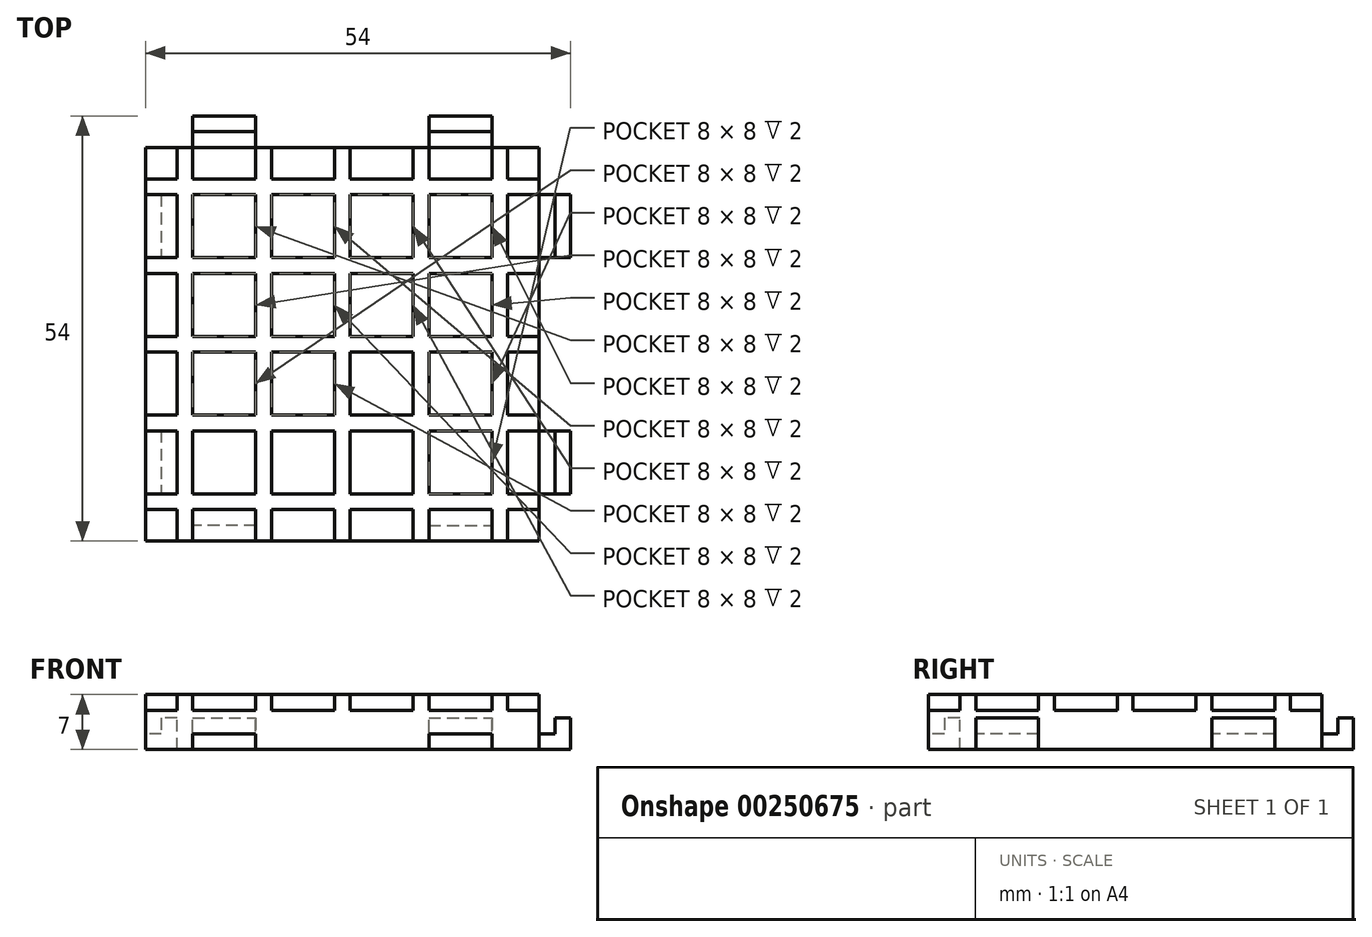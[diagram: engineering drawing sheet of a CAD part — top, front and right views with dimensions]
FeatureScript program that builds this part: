
annotation { "Feature Type Name" : "Feature", "Feature Type Description" : "" }
export const myFeature = defineFeature(function(context is Context, id is Id, definition is map)
    precondition{}
    {
        {
            var Q0;
            Q0=qCreatedBy(makeId("Top.planeOp"),FACE);
            var sketch = newSketch(context, id + "F0", { "sketchPlane" : qUnion([Q0])});
            skLineSegment(sketch, "E0.bottom", {"start": v(-29.37, 40.47) * mm, "end": v(20.63, 40.47) * mm});
            skLineSegment(sketch, "E0.top", {"start": v(-29.37, -9.53) * mm, "end": v(20.63, -9.53) * mm});
            skLineSegment(sketch, "E0.left", {"start": v(-29.37, 40.47) * mm, "end": v(-29.37, -9.53) * mm});
            skLineSegment(sketch, "E0.right", {"start": v(20.63, 40.47) * mm, "end": v(20.63, -9.53) * mm});
            skSolve(sketch);
        }
        {
            var Q0;
            Q0 = qSketchRegion(id + "F0", true);
            extrude(context, id + "F1", {"entities" : qUnion([Q0]), "depth" : 5 * mm});
        }
        {
            var Q0;
            Q0=makeQuery(id+"F1.opExtrude","CAP_FACE",FACE,{"disambiguationData":[OSD([sQuery(id+"F0.wireOp",EDGE,"E0.bottom"),sQuery(id+"F0.wireOp",EDGE,"E0.top"),sQuery(id+"F0.wireOp",EDGE,"E0.left"),sQuery(id+"F0.wireOp",EDGE,"E0.right")])],"isStart":false});
            var sketch = newSketch(context, id + "F2", { "sketchPlane" : qUnion([Q0])});
            skLineSegment(sketch, "E1.bottom", {"start": v(-29.37, -5.53) * mm, "end": v(20.63, -5.53) * mm});
            skLineSegment(sketch, "E1.top", {"start": v(-29.37, -3.53) * mm, "end": v(20.63, -3.53) * mm});
            skLineSegment(sketch, "E1.left", {"start": v(-29.37, -5.53) * mm, "end": v(-29.37, -3.53) * mm});
            skLineSegment(sketch, "E1.right", {"start": v(20.63, -5.53) * mm, "end": v(20.63, -3.53) * mm});
            skLineSegment(sketch, "E2.bottom", {"start": v(-29.37, 4.47) * mm, "end": v(20.63, 4.47) * mm});
            skLineSegment(sketch, "E2.top", {"start": v(-29.37, 6.47) * mm, "end": v(20.63, 6.47) * mm});
            skLineSegment(sketch, "E2.left", {"start": v(-29.37, 4.47) * mm, "end": v(-29.37, 6.47) * mm});
            skLineSegment(sketch, "E2.right", {"start": v(20.63, 4.47) * mm, "end": v(20.63, 6.47) * mm});
            skLineSegment(sketch, "E3.bottom", {"start": v(-29.37, 14.47) * mm, "end": v(20.63, 14.47) * mm});
            skLineSegment(sketch, "E3.top", {"start": v(-29.37, 16.47) * mm, "end": v(20.63, 16.47) * mm});
            skLineSegment(sketch, "E3.left", {"start": v(-29.37, 14.47) * mm, "end": v(-29.37, 16.47) * mm});
            skLineSegment(sketch, "E3.right", {"start": v(20.63, 14.47) * mm, "end": v(20.63, 16.47) * mm});
            skLineSegment(sketch, "E4.bottom", {"start": v(-29.37, 24.47) * mm, "end": v(20.63, 24.47) * mm});
            skLineSegment(sketch, "E4.top", {"start": v(-29.37, 26.47) * mm, "end": v(20.63, 26.47) * mm});
            skLineSegment(sketch, "E4.left", {"start": v(-29.37, 24.47) * mm, "end": v(-29.37, 26.47) * mm});
            skLineSegment(sketch, "E4.right", {"start": v(20.63, 24.47) * mm, "end": v(20.63, 26.47) * mm});
            skLineSegment(sketch, "E5.bottom", {"start": v(-29.37, 34.47) * mm, "end": v(20.63, 34.47) * mm});
            skLineSegment(sketch, "E5.top", {"start": v(-29.37, 36.47) * mm, "end": v(20.63, 36.47) * mm});
            skLineSegment(sketch, "E5.left", {"start": v(-29.37, 34.47) * mm, "end": v(-29.37, 36.47) * mm});
            skLineSegment(sketch, "E5.right", {"start": v(20.63, 34.47) * mm, "end": v(20.63, 36.47) * mm});
            skLineSegment(sketch, "E6.bottom", {"start": v(-25.37, -9.53) * mm, "end": v(-23.37, -9.53) * mm});
            skLineSegment(sketch, "E6.top", {"start": v(-25.37, 40.47) * mm, "end": v(-23.37, 40.47) * mm});
            skLineSegment(sketch, "E6.left", {"start": v(-25.37, -9.53) * mm, "end": v(-25.37, 40.47) * mm});
            skLineSegment(sketch, "E6.right", {"start": v(-23.37, -9.53) * mm, "end": v(-23.37, 40.47) * mm});
            skLineSegment(sketch, "E7.bottom", {"start": v(-15.37, -9.53) * mm, "end": v(-13.37, -9.53) * mm});
            skLineSegment(sketch, "E7.top", {"start": v(-15.37, 40.47) * mm, "end": v(-13.37, 40.47) * mm});
            skLineSegment(sketch, "E7.left", {"start": v(-15.37, -9.53) * mm, "end": v(-15.37, 40.47) * mm});
            skLineSegment(sketch, "E7.right", {"start": v(-13.37, -9.53) * mm, "end": v(-13.37, 40.47) * mm});
            skLineSegment(sketch, "E8.bottom", {"start": v(-5.37, -9.53) * mm, "end": v(-3.37, -9.53) * mm});
            skLineSegment(sketch, "E8.top", {"start": v(-5.37, 40.47) * mm, "end": v(-3.37, 40.47) * mm});
            skLineSegment(sketch, "E8.left", {"start": v(-5.37, -9.53) * mm, "end": v(-5.37, 40.47) * mm});
            skLineSegment(sketch, "E8.right", {"start": v(-3.37, -9.53) * mm, "end": v(-3.37, 40.47) * mm});
            skLineSegment(sketch, "E9.bottom", {"start": v(4.63, -9.53) * mm, "end": v(6.63, -9.53) * mm});
            skLineSegment(sketch, "E9.top", {"start": v(4.63, 40.47) * mm, "end": v(6.63, 40.47) * mm});
            skLineSegment(sketch, "E9.left", {"start": v(4.63, -9.53) * mm, "end": v(4.63, 40.47) * mm});
            skLineSegment(sketch, "E9.right", {"start": v(6.63, -9.53) * mm, "end": v(6.63, 40.47) * mm});
            skLineSegment(sketch, "E10.bottom", {"start": v(14.63, -9.53) * mm, "end": v(16.63, -9.53) * mm});
            skLineSegment(sketch, "E10.top", {"start": v(14.63, 40.47) * mm, "end": v(16.63, 40.47) * mm});
            skLineSegment(sketch, "E10.left", {"start": v(14.63, -9.53) * mm, "end": v(14.63, 40.47) * mm});
            skLineSegment(sketch, "E10.right", {"start": v(16.63, -9.53) * mm, "end": v(16.63, 40.47) * mm});
            skSolve(sketch);
        }
        {
            var Q0;
            Q0=makeQuery(id+"F4.boolean.opBoolean","MERGE",FACE,{"derivedFrom":[makeQuery(id+"F1.opExtrude","SWEPT_FACE",FACE,{"disambiguationData":[OSD([sQuery(id+"F0.wireOp",EDGE,"E0.top")])]}),makeQuery(id+"F4.opExtrude","SWEPT_FACE",FACE,{"disambiguationData":[OSD([sQuery(id+"F2.wireOp",EDGE,"E6.bottom")])]}),makeQuery(id+"F4.opExtrude","SWEPT_FACE",FACE,{"disambiguationData":[OSD([sQuery(id+"F2.wireOp",EDGE,"E7.bottom")])]}),makeQuery(id+"F4.opExtrude","SWEPT_FACE",FACE,{"disambiguationData":[OSD([sQuery(id+"F2.wireOp",EDGE,"E8.bottom")])]}),makeQuery(id+"F4.opExtrude","SWEPT_FACE",FACE,{"disambiguationData":[OSD([sQuery(id+"F2.wireOp",EDGE,"E9.bottom")])]}),makeQuery(id+"F4.opExtrude","SWEPT_FACE",FACE,{"disambiguationData":[OSD([sQuery(id+"F2.wireOp",EDGE,"E10.bottom")])]})]});
            var sketch = newSketch(context, id + "F3", { "sketchPlane" : qUnion([Q0])});
            skLineSegment(sketch, "E11.bottom", {"start": v(-23.37, 0) * mm, "end": v(-15.37, 0) * mm});
            skLineSegment(sketch, "E11.top", {"start": v(-23.37, 2) * mm, "end": v(-15.37, 2) * mm});
            skLineSegment(sketch, "E11.left", {"start": v(-23.37, 0) * mm, "end": v(-23.37, 2) * mm});
            skLineSegment(sketch, "E11.right", {"start": v(-15.37, 0) * mm, "end": v(-15.37, 2) * mm});
            skLineSegment(sketch, "E12.bottom", {"start": v(6.63, 0) * mm, "end": v(14.63, 0) * mm});
            skLineSegment(sketch, "E12.top", {"start": v(6.63, 2) * mm, "end": v(14.63, 2) * mm});
            skLineSegment(sketch, "E12.left", {"start": v(6.63, 0) * mm, "end": v(6.63, 2) * mm});
            skLineSegment(sketch, "E12.right", {"start": v(14.63, 0) * mm, "end": v(14.63, 2) * mm});
            skSolve(sketch);
        }
        {
            var Q0;
            Q0 = qSketchRegion(id + "F2", true);
            var Q1;
            {var subQ0=sQuery(id+"F2.wireOp",EDGE,"E7.left");var subQ1=sQuery(id+"F2.wireOp",EDGE,"E1.top");var subQ2=makeQuery(id+"F2.imprint","INTERSECT",VERTEX,{"derivedFrom":[subQ1,subQ0]});Q1=makeQuery(id+"F2.imprint","IMPRINT",FACE,{"disambiguationData":[TD([[makeQuery(id+"F2.imprint","IMPRINT",EDGE,{"disambiguationData":[TD([[subQ2,-1.0]])],"derivedFrom":subQ1}),1.0]])]});}
            var Q2;
            {var subQ0=sQuery(id+"F2.wireOp",EDGE,"E7.left");var subQ1=sQuery(id+"F2.wireOp",EDGE,"E2.bottom");var subQ2=makeQuery(id+"F2.imprint","INTERSECT",VERTEX,{"derivedFrom":[subQ1,subQ0]});Q2=makeQuery(id+"F2.imprint","IMPRINT",FACE,{"disambiguationData":[TD([[makeQuery(id+"F2.imprint","IMPRINT",EDGE,{"disambiguationData":[TD([[subQ2,-1.0]])],"derivedFrom":subQ1}),1.0]])]});}
            var Q3;
            {var subQ0=sQuery(id+"F2.wireOp",EDGE,"E7.right");var subQ1=sQuery(id+"F2.wireOp",EDGE,"E2.bottom");var subQ2=makeQuery(id+"F2.imprint","INTERSECT",VERTEX,{"derivedFrom":[subQ1,subQ0]});Q3=makeQuery(id+"F2.imprint","IMPRINT",FACE,{"disambiguationData":[TD([[makeQuery(id+"F2.imprint","IMPRINT",EDGE,{"disambiguationData":[TD([[subQ2,-1.0]])],"derivedFrom":subQ1}),1.0]])]});}
            var Q4;
            {var subQ0=sQuery(id+"F2.wireOp",EDGE,"E7.left");var subQ1=sQuery(id+"F2.wireOp",EDGE,"E2.top");var subQ2=makeQuery(id+"F2.imprint","INTERSECT",VERTEX,{"derivedFrom":[subQ1,subQ0]});Q4=makeQuery(id+"F2.imprint","IMPRINT",FACE,{"disambiguationData":[TD([[makeQuery(id+"F2.imprint","IMPRINT",EDGE,{"disambiguationData":[TD([[subQ2,-1.0]])],"derivedFrom":subQ1}),1.0]])]});}
            var Q5;
            {var subQ0=sQuery(id+"F2.wireOp",EDGE,"E7.left");var subQ1=sQuery(id+"F2.wireOp",EDGE,"E3.bottom");var subQ2=makeQuery(id+"F2.imprint","INTERSECT",VERTEX,{"derivedFrom":[subQ1,subQ0]});Q5=makeQuery(id+"F2.imprint","IMPRINT",FACE,{"disambiguationData":[TD([[makeQuery(id+"F2.imprint","IMPRINT",EDGE,{"disambiguationData":[TD([[subQ2,-1.0]])],"derivedFrom":subQ1}),1.0]])]});}
            var Q6;
            {var subQ0=sQuery(id+"F2.wireOp",EDGE,"E6.right");var subQ1=sQuery(id+"F2.wireOp",EDGE,"E3.bottom");var subQ2=makeQuery(id+"F2.imprint","INTERSECT",VERTEX,{"derivedFrom":[subQ1,subQ0]});Q6=makeQuery(id+"F2.imprint","IMPRINT",FACE,{"disambiguationData":[TD([[makeQuery(id+"F2.imprint","IMPRINT",EDGE,{"disambiguationData":[TD([[subQ2,-1.0]])],"derivedFrom":subQ1}),1.0]])]});}
            var Q7;
            {var subQ0=sQuery(id+"F2.wireOp",EDGE,"E6.right");var subQ1=sQuery(id+"F2.wireOp",EDGE,"E4.bottom");var subQ2=makeQuery(id+"F2.imprint","INTERSECT",VERTEX,{"derivedFrom":[subQ1,subQ0]});Q7=makeQuery(id+"F2.imprint","IMPRINT",FACE,{"disambiguationData":[TD([[makeQuery(id+"F2.imprint","IMPRINT",EDGE,{"disambiguationData":[TD([[subQ2,-1.0]])],"derivedFrom":subQ1}),1.0]])]});}
            var Q8;
            {var subQ0=sQuery(id+"F2.wireOp",EDGE,"E7.left");var subQ1=sQuery(id+"F2.wireOp",EDGE,"E4.bottom");var subQ2=makeQuery(id+"F2.imprint","INTERSECT",VERTEX,{"derivedFrom":[subQ1,subQ0]});Q8=makeQuery(id+"F2.imprint","IMPRINT",FACE,{"disambiguationData":[TD([[makeQuery(id+"F2.imprint","IMPRINT",EDGE,{"disambiguationData":[TD([[subQ2,-1.0]])],"derivedFrom":subQ1}),1.0]])]});}
            var Q9;
            {var subQ0=sQuery(id+"F2.wireOp",EDGE,"E7.left");var subQ1=sQuery(id+"F2.wireOp",EDGE,"E4.top");var subQ2=makeQuery(id+"F2.imprint","INTERSECT",VERTEX,{"derivedFrom":[subQ1,subQ0]});Q9=makeQuery(id+"F2.imprint","IMPRINT",FACE,{"disambiguationData":[TD([[makeQuery(id+"F2.imprint","IMPRINT",EDGE,{"disambiguationData":[TD([[subQ2,-1.0]])],"derivedFrom":subQ1}),1.0]])]});}
            var Q10;
            {var subQ0=sQuery(id+"F2.wireOp",EDGE,"E7.left");var subQ1=sQuery(id+"F2.wireOp",EDGE,"E3.top");var subQ2=makeQuery(id+"F2.imprint","INTERSECT",VERTEX,{"derivedFrom":[subQ1,subQ0]});Q10=makeQuery(id+"F2.imprint","IMPRINT",FACE,{"disambiguationData":[TD([[makeQuery(id+"F2.imprint","IMPRINT",EDGE,{"disambiguationData":[TD([[subQ2,-1.0]])],"derivedFrom":subQ1}),1.0]])]});}
            var Q11;
            {var subQ0=sQuery(id+"F2.wireOp",EDGE,"E7.right");var subQ1=sQuery(id+"F2.wireOp",EDGE,"E4.bottom");var subQ2=makeQuery(id+"F2.imprint","INTERSECT",VERTEX,{"derivedFrom":[subQ1,subQ0]});Q11=makeQuery(id+"F2.imprint","IMPRINT",FACE,{"disambiguationData":[TD([[makeQuery(id+"F2.imprint","IMPRINT",EDGE,{"disambiguationData":[TD([[subQ2,-1.0]])],"derivedFrom":subQ1}),1.0]])]});}
            var Q12;
            {var subQ0=sQuery(id+"F2.wireOp",EDGE,"E8.left");var subQ1=sQuery(id+"F2.wireOp",EDGE,"E3.top");var subQ2=makeQuery(id+"F2.imprint","INTERSECT",VERTEX,{"derivedFrom":[subQ1,subQ0]});Q12=makeQuery(id+"F2.imprint","IMPRINT",FACE,{"disambiguationData":[TD([[makeQuery(id+"F2.imprint","IMPRINT",EDGE,{"disambiguationData":[TD([[subQ2,-1.0]])],"derivedFrom":subQ1}),1.0]])]});}
            var Q13;
            {var subQ0=sQuery(id+"F2.wireOp",EDGE,"E8.left");var subQ1=sQuery(id+"F2.wireOp",EDGE,"E3.bottom");var subQ2=makeQuery(id+"F2.imprint","INTERSECT",VERTEX,{"derivedFrom":[subQ1,subQ0]});Q13=makeQuery(id+"F2.imprint","IMPRINT",FACE,{"disambiguationData":[TD([[makeQuery(id+"F2.imprint","IMPRINT",EDGE,{"disambiguationData":[TD([[subQ2,-1.0]])],"derivedFrom":subQ1}),1.0]])]});}
            var Q14;
            {var subQ0=sQuery(id+"F2.wireOp",EDGE,"E7.right");var subQ1=sQuery(id+"F2.wireOp",EDGE,"E3.bottom");var subQ2=makeQuery(id+"F2.imprint","INTERSECT",VERTEX,{"derivedFrom":[subQ1,subQ0]});Q14=makeQuery(id+"F2.imprint","IMPRINT",FACE,{"disambiguationData":[TD([[makeQuery(id+"F2.imprint","IMPRINT",EDGE,{"disambiguationData":[TD([[subQ2,-1.0]])],"derivedFrom":subQ1}),1.0]])]});}
            var Q15;
            {var subQ0=sQuery(id+"F2.wireOp",EDGE,"E8.left");var subQ1=sQuery(id+"F2.wireOp",EDGE,"E2.top");var subQ2=makeQuery(id+"F2.imprint","INTERSECT",VERTEX,{"derivedFrom":[subQ1,subQ0]});Q15=makeQuery(id+"F2.imprint","IMPRINT",FACE,{"disambiguationData":[TD([[makeQuery(id+"F2.imprint","IMPRINT",EDGE,{"disambiguationData":[TD([[subQ2,-1.0]])],"derivedFrom":subQ1}),1.0]])]});}
            var Q16;
            {var subQ0=sQuery(id+"F2.wireOp",EDGE,"E8.left");var subQ1=sQuery(id+"F2.wireOp",EDGE,"E2.bottom");var subQ2=makeQuery(id+"F2.imprint","INTERSECT",VERTEX,{"derivedFrom":[subQ1,subQ0]});Q16=makeQuery(id+"F2.imprint","IMPRINT",FACE,{"disambiguationData":[TD([[makeQuery(id+"F2.imprint","IMPRINT",EDGE,{"disambiguationData":[TD([[subQ2,-1.0]])],"derivedFrom":subQ1}),1.0]])]});}
            var Q17;
            {var subQ0=sQuery(id+"F2.wireOp",EDGE,"E8.left");var subQ1=sQuery(id+"F2.wireOp",EDGE,"E1.top");var subQ2=makeQuery(id+"F2.imprint","INTERSECT",VERTEX,{"derivedFrom":[subQ1,subQ0]});Q17=makeQuery(id+"F2.imprint","IMPRINT",FACE,{"disambiguationData":[TD([[makeQuery(id+"F2.imprint","IMPRINT",EDGE,{"disambiguationData":[TD([[subQ2,-1.0]])],"derivedFrom":subQ1}),1.0]])]});}
            var Q18;
            {var subQ0=sQuery(id+"F2.wireOp",EDGE,"E8.right");var subQ1=sQuery(id+"F2.wireOp",EDGE,"E2.bottom");var subQ2=makeQuery(id+"F2.imprint","INTERSECT",VERTEX,{"derivedFrom":[subQ1,subQ0]});Q18=makeQuery(id+"F2.imprint","IMPRINT",FACE,{"disambiguationData":[TD([[makeQuery(id+"F2.imprint","IMPRINT",EDGE,{"disambiguationData":[TD([[subQ2,-1.0]])],"derivedFrom":subQ1}),1.0]])]});}
            var Q19;
            {var subQ0=sQuery(id+"F2.wireOp",EDGE,"E9.left");var subQ1=sQuery(id+"F2.wireOp",EDGE,"E1.top");var subQ2=makeQuery(id+"F2.imprint","INTERSECT",VERTEX,{"derivedFrom":[subQ1,subQ0]});Q19=makeQuery(id+"F2.imprint","IMPRINT",FACE,{"disambiguationData":[TD([[makeQuery(id+"F2.imprint","IMPRINT",EDGE,{"disambiguationData":[TD([[subQ2,-1.0]])],"derivedFrom":subQ1}),1.0]])]});}
            var Q20;
            {var subQ0=sQuery(id+"F2.wireOp",EDGE,"E9.left");var subQ1=sQuery(id+"F2.wireOp",EDGE,"E2.bottom");var subQ2=makeQuery(id+"F2.imprint","INTERSECT",VERTEX,{"derivedFrom":[subQ1,subQ0]});Q20=makeQuery(id+"F2.imprint","IMPRINT",FACE,{"disambiguationData":[TD([[makeQuery(id+"F2.imprint","IMPRINT",EDGE,{"disambiguationData":[TD([[subQ2,-1.0]])],"derivedFrom":subQ1}),1.0]])]});}
            var Q21;
            {var subQ0=sQuery(id+"F2.wireOp",EDGE,"E9.right");var subQ1=sQuery(id+"F2.wireOp",EDGE,"E2.bottom");var subQ2=makeQuery(id+"F2.imprint","INTERSECT",VERTEX,{"derivedFrom":[subQ1,subQ0]});Q21=makeQuery(id+"F2.imprint","IMPRINT",FACE,{"disambiguationData":[TD([[makeQuery(id+"F2.imprint","IMPRINT",EDGE,{"disambiguationData":[TD([[subQ2,-1.0]])],"derivedFrom":subQ1}),1.0]])]});}
            var Q22;
            {var subQ0=sQuery(id+"F2.wireOp",EDGE,"E9.left");var subQ1=sQuery(id+"F2.wireOp",EDGE,"E2.top");var subQ2=makeQuery(id+"F2.imprint","INTERSECT",VERTEX,{"derivedFrom":[subQ1,subQ0]});Q22=makeQuery(id+"F2.imprint","IMPRINT",FACE,{"disambiguationData":[TD([[makeQuery(id+"F2.imprint","IMPRINT",EDGE,{"disambiguationData":[TD([[subQ2,-1.0]])],"derivedFrom":subQ1}),1.0]])]});}
            var Q23;
            {var subQ0=sQuery(id+"F2.wireOp",EDGE,"E9.right");var subQ1=sQuery(id+"F2.wireOp",EDGE,"E3.bottom");var subQ2=makeQuery(id+"F2.imprint","INTERSECT",VERTEX,{"derivedFrom":[subQ1,subQ0]});Q23=makeQuery(id+"F2.imprint","IMPRINT",FACE,{"disambiguationData":[TD([[makeQuery(id+"F2.imprint","IMPRINT",EDGE,{"disambiguationData":[TD([[subQ2,-1.0]])],"derivedFrom":subQ1}),1.0]])]});}
            var Q24;
            {var subQ0=sQuery(id+"F2.wireOp",EDGE,"E9.left");var subQ1=sQuery(id+"F2.wireOp",EDGE,"E3.bottom");var subQ2=makeQuery(id+"F2.imprint","INTERSECT",VERTEX,{"derivedFrom":[subQ1,subQ0]});Q24=makeQuery(id+"F2.imprint","IMPRINT",FACE,{"disambiguationData":[TD([[makeQuery(id+"F2.imprint","IMPRINT",EDGE,{"disambiguationData":[TD([[subQ2,-1.0]])],"derivedFrom":subQ1}),1.0]])]});}
            var Q25;
            {var subQ0=sQuery(id+"F2.wireOp",EDGE,"E8.right");var subQ1=sQuery(id+"F2.wireOp",EDGE,"E3.bottom");var subQ2=makeQuery(id+"F2.imprint","INTERSECT",VERTEX,{"derivedFrom":[subQ1,subQ0]});Q25=makeQuery(id+"F2.imprint","IMPRINT",FACE,{"disambiguationData":[TD([[makeQuery(id+"F2.imprint","IMPRINT",EDGE,{"disambiguationData":[TD([[subQ2,-1.0]])],"derivedFrom":subQ1}),1.0]])]});}
            var Q26;
            {var subQ0=sQuery(id+"F2.wireOp",EDGE,"E9.left");var subQ1=sQuery(id+"F2.wireOp",EDGE,"E3.top");var subQ2=makeQuery(id+"F2.imprint","INTERSECT",VERTEX,{"derivedFrom":[subQ1,subQ0]});Q26=makeQuery(id+"F2.imprint","IMPRINT",FACE,{"disambiguationData":[TD([[makeQuery(id+"F2.imprint","IMPRINT",EDGE,{"disambiguationData":[TD([[subQ2,-1.0]])],"derivedFrom":subQ1}),1.0]])]});}
            var Q27;
            {var subQ0=sQuery(id+"F2.wireOp",EDGE,"E9.left");var subQ1=sQuery(id+"F2.wireOp",EDGE,"E4.bottom");var subQ2=makeQuery(id+"F2.imprint","INTERSECT",VERTEX,{"derivedFrom":[subQ1,subQ0]});Q27=makeQuery(id+"F2.imprint","IMPRINT",FACE,{"disambiguationData":[TD([[makeQuery(id+"F2.imprint","IMPRINT",EDGE,{"disambiguationData":[TD([[subQ2,-1.0]])],"derivedFrom":subQ1}),1.0]])]});}
            var Q28;
            {var subQ0=sQuery(id+"F2.wireOp",EDGE,"E8.right");var subQ1=sQuery(id+"F2.wireOp",EDGE,"E4.bottom");var subQ2=makeQuery(id+"F2.imprint","INTERSECT",VERTEX,{"derivedFrom":[subQ1,subQ0]});Q28=makeQuery(id+"F2.imprint","IMPRINT",FACE,{"disambiguationData":[TD([[makeQuery(id+"F2.imprint","IMPRINT",EDGE,{"disambiguationData":[TD([[subQ2,-1.0]])],"derivedFrom":subQ1}),1.0]])]});}
            var Q29;
            {var subQ0=sQuery(id+"F2.wireOp",EDGE,"E8.left");var subQ1=sQuery(id+"F2.wireOp",EDGE,"E4.top");var subQ2=makeQuery(id+"F2.imprint","INTERSECT",VERTEX,{"derivedFrom":[subQ1,subQ0]});Q29=makeQuery(id+"F2.imprint","IMPRINT",FACE,{"disambiguationData":[TD([[makeQuery(id+"F2.imprint","IMPRINT",EDGE,{"disambiguationData":[TD([[subQ2,-1.0]])],"derivedFrom":subQ1}),1.0]])]});}
            var Q30;
            {var subQ0=sQuery(id+"F2.wireOp",EDGE,"E8.left");var subQ1=sQuery(id+"F2.wireOp",EDGE,"E4.bottom");var subQ2=makeQuery(id+"F2.imprint","INTERSECT",VERTEX,{"derivedFrom":[subQ1,subQ0]});Q30=makeQuery(id+"F2.imprint","IMPRINT",FACE,{"disambiguationData":[TD([[makeQuery(id+"F2.imprint","IMPRINT",EDGE,{"disambiguationData":[TD([[subQ2,-1.0]])],"derivedFrom":subQ1}),1.0]])]});}
            var Q31;
            {var subQ0=sQuery(id+"F2.wireOp",EDGE,"E9.left");var subQ1=sQuery(id+"F2.wireOp",EDGE,"E4.top");var subQ2=makeQuery(id+"F2.imprint","INTERSECT",VERTEX,{"derivedFrom":[subQ1,subQ0]});Q31=makeQuery(id+"F2.imprint","IMPRINT",FACE,{"disambiguationData":[TD([[makeQuery(id+"F2.imprint","IMPRINT",EDGE,{"disambiguationData":[TD([[subQ2,-1.0]])],"derivedFrom":subQ1}),1.0]])]});}
            var Q32;
            {var subQ0=sQuery(id+"F2.wireOp",EDGE,"E9.right");var subQ1=sQuery(id+"F2.wireOp",EDGE,"E4.bottom");var subQ2=makeQuery(id+"F2.imprint","INTERSECT",VERTEX,{"derivedFrom":[subQ1,subQ0]});Q32=makeQuery(id+"F2.imprint","IMPRINT",FACE,{"disambiguationData":[TD([[makeQuery(id+"F2.imprint","IMPRINT",EDGE,{"disambiguationData":[TD([[subQ2,-1.0]])],"derivedFrom":subQ1}),1.0]])]});}
            var Q33;
            {var subQ0=sQuery(id+"F2.wireOp",EDGE,"E6.right");var subQ1=sQuery(id+"F2.wireOp",EDGE,"E2.bottom");var subQ2=makeQuery(id+"F2.imprint","INTERSECT",VERTEX,{"derivedFrom":[subQ1,subQ0]});Q33=makeQuery(id+"F2.imprint","IMPRINT",FACE,{"disambiguationData":[TD([[makeQuery(id+"F2.imprint","IMPRINT",EDGE,{"disambiguationData":[TD([[subQ2,-1.0]])],"derivedFrom":subQ1}),1.0]])]});}
            extrude(context, id + "F4", {"entities" : qUnion([Q0, Q1, Q2, Q3, Q4, Q5, Q6, Q7, Q8, Q9, Q10, Q11, Q12, Q13, Q14, Q15, Q16, Q17, Q18, Q19, Q20, Q21, Q22, Q23, Q24, Q25, Q26, Q27, Q28, Q29, Q30, Q31, Q32, Q33]), "operationType" : NewBodyOperationType.ADD, "depth" : 2 * mm});
        }
        {
            var Q0;
            Q0 = qSketchRegion(id + "F3", true);
            extrude(context, id + "F5", {"entities" : qUnion([Q0]), "operationType" : NewBodyOperationType.REMOVE, "oppositeDirection" : true, "depth" : 4 * mm});
        }
        {
            var Q0;
            Q0=makeQuery(id+"F4.boolean.opBoolean","MERGE",FACE,{"derivedFrom":[makeQuery(id+"F1.opExtrude","SWEPT_FACE",FACE,{"disambiguationData":[OSD([sQuery(id+"F0.wireOp",EDGE,"E0.left")])]}),makeQuery(id+"F4.opExtrude","SWEPT_FACE",FACE,{"disambiguationData":[OSD([sQuery(id+"F2.wireOp",EDGE,"E1.left")])]}),makeQuery(id+"F4.opExtrude","SWEPT_FACE",FACE,{"disambiguationData":[OSD([sQuery(id+"F2.wireOp",EDGE,"E2.left")])]}),makeQuery(id+"F4.opExtrude","SWEPT_FACE",FACE,{"disambiguationData":[OSD([sQuery(id+"F2.wireOp",EDGE,"E3.left")])]}),makeQuery(id+"F4.opExtrude","SWEPT_FACE",FACE,{"disambiguationData":[OSD([sQuery(id+"F2.wireOp",EDGE,"E4.left")])]}),makeQuery(id+"F4.opExtrude","SWEPT_FACE",FACE,{"disambiguationData":[OSD([sQuery(id+"F2.wireOp",EDGE,"E5.left")])]})]});
            var sketch = newSketch(context, id + "F6", { "sketchPlane" : qUnion([Q0])});
            skLineSegment(sketch, "E13.bottom", {"start": v(-34.47, 0) * mm, "end": v(-26.47, 0) * mm});
            skLineSegment(sketch, "E13.top", {"start": v(-34.47, 2) * mm, "end": v(-26.47, 2) * mm});
            skLineSegment(sketch, "E13.left", {"start": v(-34.47, 0) * mm, "end": v(-34.47, 2) * mm});
            skLineSegment(sketch, "E13.right", {"start": v(-26.47, 0) * mm, "end": v(-26.47, 2) * mm});
            skLineSegment(sketch, "E14.bottom", {"start": v(-4.47, 0) * mm, "end": v(3.53, 0) * mm});
            skLineSegment(sketch, "E14.top", {"start": v(-4.47, 2) * mm, "end": v(3.53, 2) * mm});
            skLineSegment(sketch, "E14.left", {"start": v(-4.47, 0) * mm, "end": v(-4.47, 2) * mm});
            skLineSegment(sketch, "E14.right", {"start": v(3.53, 0) * mm, "end": v(3.53, 2) * mm});
            skSolve(sketch);
        }
        {
            var Q0;
            Q0 = qSketchRegion(id + "F6", true);
            extrude(context, id + "F7", {"entities" : qUnion([Q0]), "operationType" : NewBodyOperationType.REMOVE, "oppositeDirection" : true, "depth" : 4 * mm});
        }
        {
            var Q0;
            Q0=makeQuery(id+"F4.boolean.opBoolean","MERGE",FACE,{"derivedFrom":[makeQuery(id+"F1.opExtrude","SWEPT_FACE",FACE,{"disambiguationData":[OSD([sQuery(id+"F0.wireOp",EDGE,"E0.bottom")])]}),makeQuery(id+"F4.opExtrude","SWEPT_FACE",FACE,{"disambiguationData":[OSD([sQuery(id+"F2.wireOp",EDGE,"E6.top")])]}),makeQuery(id+"F4.opExtrude","SWEPT_FACE",FACE,{"disambiguationData":[OSD([sQuery(id+"F2.wireOp",EDGE,"E7.top")])]}),makeQuery(id+"F4.opExtrude","SWEPT_FACE",FACE,{"disambiguationData":[OSD([sQuery(id+"F2.wireOp",EDGE,"E8.top")])]}),makeQuery(id+"F4.opExtrude","SWEPT_FACE",FACE,{"disambiguationData":[OSD([sQuery(id+"F2.wireOp",EDGE,"E9.top")])]}),makeQuery(id+"F4.opExtrude","SWEPT_FACE",FACE,{"disambiguationData":[OSD([sQuery(id+"F2.wireOp",EDGE,"E10.top")])]})]});
            var sketch = newSketch(context, id + "F8", { "sketchPlane" : qUnion([Q0])});
            skLineSegment(sketch, "E15.bottom", {"start": v(-14.63, 0) * mm, "end": v(-6.63, 0) * mm});
            skLineSegment(sketch, "E15.top", {"start": v(-14.63, 2) * mm, "end": v(-6.63, 2) * mm});
            skLineSegment(sketch, "E15.left", {"start": v(-14.63, 0) * mm, "end": v(-14.63, 2) * mm});
            skLineSegment(sketch, "E15.right", {"start": v(-6.63, 0) * mm, "end": v(-6.63, 2) * mm});
            skLineSegment(sketch, "E16.bottom", {"start": v(15.37, 0) * mm, "end": v(23.37, 0) * mm});
            skLineSegment(sketch, "E16.top", {"start": v(15.37, 2) * mm, "end": v(23.37, 2) * mm});
            skLineSegment(sketch, "E16.left", {"start": v(15.37, 0) * mm, "end": v(15.37, 2) * mm});
            skLineSegment(sketch, "E16.right", {"start": v(23.37, 0) * mm, "end": v(23.37, 2) * mm});
            skSolve(sketch);
        }
        {
            var Q0;
            Q0 = qSketchRegion(id + "F8", true);
            extrude(context, id + "F9", {"entities" : qUnion([Q0]), "operationType" : NewBodyOperationType.ADD, "depth" : 4 * mm});
        }
        {
            var Q0;
            Q0=makeQuery(id+"F9.opExtrude","SWEPT_FACE",FACE,{"disambiguationData":[OSD([sQuery(id+"F8.wireOp",EDGE,"E16.top")])]});
            var sketch = newSketch(context, id + "F10", { "sketchPlane" : qUnion([Q0])});
            skLineSegment(sketch, "E17.bottom", {"start": v(-23.37, 44.47) * mm, "end": v(-15.37, 44.47) * mm});
            skLineSegment(sketch, "E17.top", {"start": v(-23.37, 42.47) * mm, "end": v(-15.37, 42.47) * mm});
            skLineSegment(sketch, "E17.left", {"start": v(-23.37, 44.47) * mm, "end": v(-23.37, 42.47) * mm});
            skLineSegment(sketch, "E17.right", {"start": v(-15.37, 44.47) * mm, "end": v(-15.37, 42.47) * mm});
            skSolve(sketch);
        }
        {
            var Q0;
            Q0 = qSketchRegion(id + "F10", true);
            extrude(context, id + "F11", {"entities" : qUnion([Q0]), "operationType" : NewBodyOperationType.ADD, "depth" : 2 * mm});
        }
        {
            var Q0;
            Q0=makeQuery(id+"F9.opExtrude","SWEPT_FACE",FACE,{"disambiguationData":[OSD([sQuery(id+"F8.wireOp",EDGE,"E15.top")])]});
            var sketch = newSketch(context, id + "F12", { "sketchPlane" : qUnion([Q0])});
            skLineSegment(sketch, "E18.bottom", {"start": v(6.63, 44.47) * mm, "end": v(14.63, 44.47) * mm});
            skLineSegment(sketch, "E18.top", {"start": v(6.63, 42.47) * mm, "end": v(14.63, 42.47) * mm});
            skLineSegment(sketch, "E18.left", {"start": v(6.63, 44.47) * mm, "end": v(6.63, 42.47) * mm});
            skLineSegment(sketch, "E18.right", {"start": v(14.63, 44.47) * mm, "end": v(14.63, 42.47) * mm});
            skSolve(sketch);
        }
        {
            var Q0;
            Q0 = qSketchRegion(id + "F12", true);
            extrude(context, id + "F13", {"entities" : qUnion([Q0]), "operationType" : NewBodyOperationType.ADD, "depth" : 2 * mm});
        }
        {
            var Q0;
            Q0=makeQuery(id+"F4.boolean.opBoolean","MERGE",FACE,{"derivedFrom":[makeQuery(id+"F1.opExtrude","SWEPT_FACE",FACE,{"disambiguationData":[OSD([sQuery(id+"F0.wireOp",EDGE,"E0.right")])]}),makeQuery(id+"F4.opExtrude","SWEPT_FACE",FACE,{"disambiguationData":[OSD([sQuery(id+"F2.wireOp",EDGE,"E1.right")])]}),makeQuery(id+"F4.opExtrude","SWEPT_FACE",FACE,{"disambiguationData":[OSD([sQuery(id+"F2.wireOp",EDGE,"E2.right")])]}),makeQuery(id+"F4.opExtrude","SWEPT_FACE",FACE,{"disambiguationData":[OSD([sQuery(id+"F2.wireOp",EDGE,"E3.right")])]}),makeQuery(id+"F4.opExtrude","SWEPT_FACE",FACE,{"disambiguationData":[OSD([sQuery(id+"F2.wireOp",EDGE,"E4.right")])]}),makeQuery(id+"F4.opExtrude","SWEPT_FACE",FACE,{"disambiguationData":[OSD([sQuery(id+"F2.wireOp",EDGE,"E5.right")])]})]});
            var sketch = newSketch(context, id + "F14", { "sketchPlane" : qUnion([Q0])});
            skLineSegment(sketch, "E19.bottom", {"start": v(-3.53, 0) * mm, "end": v(4.47, 0) * mm});
            skLineSegment(sketch, "E19.top", {"start": v(-3.53, 2) * mm, "end": v(4.47, 2) * mm});
            skLineSegment(sketch, "E19.left", {"start": v(-3.53, 0) * mm, "end": v(-3.53, 2) * mm});
            skLineSegment(sketch, "E19.right", {"start": v(4.47, 0) * mm, "end": v(4.47, 2) * mm});
            skLineSegment(sketch, "E20.bottom", {"start": v(26.47, 0) * mm, "end": v(34.47, 0) * mm});
            skLineSegment(sketch, "E20.top", {"start": v(26.47, 2) * mm, "end": v(34.47, 2) * mm});
            skLineSegment(sketch, "E20.left", {"start": v(26.47, 0) * mm, "end": v(26.47, 2) * mm});
            skLineSegment(sketch, "E20.right", {"start": v(34.47, 0) * mm, "end": v(34.47, 2) * mm});
            skSolve(sketch);
        }
        {
            var Q0;
            Q0 = qSketchRegion(id + "F14", true);
            extrude(context, id + "F15", {"entities" : qUnion([Q0]), "operationType" : NewBodyOperationType.ADD, "depth" : 4 * mm});
        }
        {
            var Q0;
            Q0=makeQuery(id+"F15.opExtrude","SWEPT_FACE",FACE,{"disambiguationData":[OSD([sQuery(id+"F14.wireOp",EDGE,"E20.top")])]});
            var sketch = newSketch(context, id + "F16", { "sketchPlane" : qUnion([Q0])});
            skLineSegment(sketch, "E21.bottom", {"start": v(24.63, 34.47) * mm, "end": v(22.63, 34.47) * mm});
            skLineSegment(sketch, "E21.top", {"start": v(24.63, 26.47) * mm, "end": v(22.63, 26.47) * mm});
            skLineSegment(sketch, "E21.left", {"start": v(24.63, 34.47) * mm, "end": v(24.63, 26.47) * mm});
            skLineSegment(sketch, "E21.right", {"start": v(22.63, 34.47) * mm, "end": v(22.63, 26.47) * mm});
            skSolve(sketch);
        }
        {
            var Q0;
            Q0 = qSketchRegion(id + "F16", true);
            extrude(context, id + "F17", {"entities" : qUnion([Q0]), "operationType" : NewBodyOperationType.ADD, "depth" : 2 * mm});
        }
        {
            var Q0;
            Q0=makeQuery(id+"F15.opExtrude","SWEPT_FACE",FACE,{"disambiguationData":[OSD([sQuery(id+"F14.wireOp",EDGE,"E19.top")])]});
            var sketch = newSketch(context, id + "F18", { "sketchPlane" : qUnion([Q0])});
            skLineSegment(sketch, "E22.bottom", {"start": v(24.63, 4.47) * mm, "end": v(22.63, 4.47) * mm});
            skLineSegment(sketch, "E22.top", {"start": v(24.63, -3.53) * mm, "end": v(22.63, -3.53) * mm});
            skLineSegment(sketch, "E22.left", {"start": v(24.63, 4.47) * mm, "end": v(24.63, -3.53) * mm});
            skLineSegment(sketch, "E22.right", {"start": v(22.63, 4.47) * mm, "end": v(22.63, -3.53) * mm});
            skSolve(sketch);
        }
        {
            var Q0;
            Q0 = qSketchRegion(id + "F18", true);
            extrude(context, id + "F19", {"entities" : qUnion([Q0]), "operationType" : NewBodyOperationType.ADD, "depth" : 2 * mm});
        }
        {
            var Q0;
            Q0=makeQuery(id+"F5.boolean.opBoolean","COPY",FACE,{"derivedFrom":makeQuery(id+"F5.opExtrude","SWEPT_FACE",FACE,{"disambiguationData":[OSD([sQuery(id+"F3.wireOp",EDGE,"E12.top")])]})});
            var sketch = newSketch(context, id + "F20", { "sketchPlane" : qUnion([Q0])});
            skLineSegment(sketch, "E23.bottom", {"start": v(6.63, 5.53) * mm, "end": v(14.63, 5.53) * mm});
            skLineSegment(sketch, "E23.top", {"start": v(6.63, 7.53) * mm, "end": v(14.63, 7.53) * mm});
            skLineSegment(sketch, "E23.left", {"start": v(6.63, 5.53) * mm, "end": v(6.63, 7.53) * mm});
            skLineSegment(sketch, "E23.right", {"start": v(14.63, 5.53) * mm, "end": v(14.63, 7.53) * mm});
            skSolve(sketch);
        }
        {
            var Q0;
            Q0 = qSketchRegion(id + "F20", true);
            extrude(context, id + "F21", {"entities" : qUnion([Q0]), "operationType" : NewBodyOperationType.REMOVE, "oppositeDirection" : true, "depth" : 2 * mm});
        }
        {
            var Q0;
            Q0=makeQuery(id+"F5.boolean.opBoolean","COPY",FACE,{"derivedFrom":makeQuery(id+"F5.opExtrude","SWEPT_FACE",FACE,{"disambiguationData":[OSD([sQuery(id+"F3.wireOp",EDGE,"E11.top")])]})});
            var sketch = newSketch(context, id + "F22", { "sketchPlane" : qUnion([Q0])});
            skLineSegment(sketch, "E24.bottom", {"start": v(-15.37, 5.53) * mm, "end": v(-23.37, 5.53) * mm});
            skLineSegment(sketch, "E24.top", {"start": v(-15.37, 7.53) * mm, "end": v(-23.37, 7.53) * mm});
            skLineSegment(sketch, "E24.left", {"start": v(-15.37, 5.53) * mm, "end": v(-15.37, 7.53) * mm});
            skLineSegment(sketch, "E24.right", {"start": v(-23.37, 5.53) * mm, "end": v(-23.37, 7.53) * mm});
            skSolve(sketch);
        }
        {
            var Q0;
            Q0 = qSketchRegion(id + "F22", true);
            extrude(context, id + "F23", {"entities" : qUnion([Q0]), "operationType" : NewBodyOperationType.REMOVE, "oppositeDirection" : true, "depth" : 2 * mm});
        }
        {
            var Q0;
            Q0=makeQuery(id+"F7.boolean.opBoolean","COPY",FACE,{"derivedFrom":makeQuery(id+"F7.opExtrude","SWEPT_FACE",FACE,{"disambiguationData":[OSD([sQuery(id+"F6.wireOp",EDGE,"E14.top")])]})});
            var sketch = newSketch(context, id + "F24", { "sketchPlane" : qUnion([Q0])});
            skLineSegment(sketch, "E25.bottom", {"start": v(-25.37, -4.47) * mm, "end": v(-27.37, -4.47) * mm});
            skLineSegment(sketch, "E25.top", {"start": v(-25.37, 3.53) * mm, "end": v(-27.37, 3.53) * mm});
            skLineSegment(sketch, "E25.left", {"start": v(-25.37, -4.47) * mm, "end": v(-25.37, 3.53) * mm});
            skLineSegment(sketch, "E25.right", {"start": v(-27.37, -4.47) * mm, "end": v(-27.37, 3.53) * mm});
            skSolve(sketch);
        }
        {
            var Q0;
            Q0 = qSketchRegion(id + "F24", true);
            extrude(context, id + "F25", {"entities" : qUnion([Q0]), "operationType" : NewBodyOperationType.REMOVE, "oppositeDirection" : true, "depth" : 2 * mm});
        }
        {
            var Q0;
            Q0=makeQuery(id+"F7.boolean.opBoolean","COPY",FACE,{"derivedFrom":makeQuery(id+"F7.opExtrude","SWEPT_FACE",FACE,{"disambiguationData":[OSD([sQuery(id+"F6.wireOp",EDGE,"E13.top")])]})});
            var sketch = newSketch(context, id + "F26", { "sketchPlane" : qUnion([Q0])});
            skLineSegment(sketch, "E26.bottom", {"start": v(-25.37, -34.47) * mm, "end": v(-27.37, -34.47) * mm});
            skLineSegment(sketch, "E26.top", {"start": v(-25.37, -26.47) * mm, "end": v(-27.37, -26.47) * mm});
            skLineSegment(sketch, "E26.left", {"start": v(-25.37, -34.47) * mm, "end": v(-25.37, -26.47) * mm});
            skLineSegment(sketch, "E26.right", {"start": v(-27.37, -34.47) * mm, "end": v(-27.37, -26.47) * mm});
            skSolve(sketch);
        }
        {
            var Q0;
            Q0 = qSketchRegion(id + "F26", true);
            extrude(context, id + "F27", {"entities" : qUnion([Q0]), "operationType" : NewBodyOperationType.REMOVE, "oppositeDirection" : true, "depth" : 2 * mm});
        }
    });
